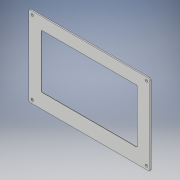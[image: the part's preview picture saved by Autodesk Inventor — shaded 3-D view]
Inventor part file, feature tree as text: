
AUTODESK INVENTOR PART (.ipt)
format: ipt  version: 2019 (Build 230136000, 136)  size: 166,912 bytes
history: native  units: in
note: dims shown in document units (in); Inventor stores cm internally (conversion verified against a paired STEP export)
features: direct_edit x2, move_body x2, extrude x1, sketch x1, imported_body x1
ambient origin geometry x8: Origin, YZ Plane, XZ Plane, XY Plane, X Axis, Y Axis, Z Axis, Center Point
bodies: Solid1 (feature_tree)
feature tree (7):
  direct_edit  "Direct Edit1"
  direct_edit  "Direct Edit2"
  extrude  "Extrusion1"  TaperAngle=0.0deg  [1 undecoded]
  sketch  "Sketch1"  dims[d0=0.0in d1=0.0in d2=0.3937in d3=0.0in d4=-0.3937in d5=0.0in d6=0.4291in d7=0.2382in d8=0.2382in d9=2.3622in d11=1.0171in d12=0.3937in d14=0.3937in d16=0.5085in d17=0.5085in d18=6.1024in d19=0.3937in d20=0.0in d21=0.8661in]
  imported_body  "Base1"
  move_body  "Move1"
  move_body  "Move2"
note: 1 required parameter value undecoded (feature->parameter linkage not recoverable at this tier; creation-order binding heuristic only, values carry confidence <= 0.55)
